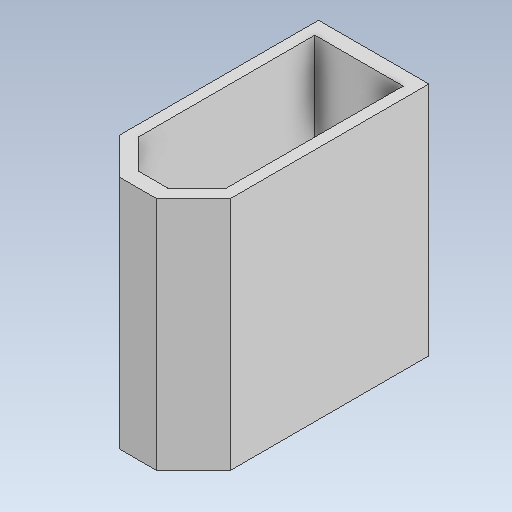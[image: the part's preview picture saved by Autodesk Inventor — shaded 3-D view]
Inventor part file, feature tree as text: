
AUTODESK INVENTOR PART (.ipt)
format: ipt  version: 2020 (Build 240168000, 168)  size: 100,352 bytes
history: native  units: in
note: dims shown in document units (in); Inventor stores cm internally (conversion verified against a paired STEP export)
features: other x3, sketch x2
ambient origin geometry x8: Origin, YZ Plane, XZ Plane, XY Plane, X Axis, Y Axis, Z Axis, Center Point
bodies: Solid1 (feature_tree)
feature tree (5):
  other  "TX60.ipt"
  other  "Solid1::TX60.ipt"
  other  "TaggingFeature1"
  sketch  "Sketch1"  dims[d0=0.3937in]
  sketch  "Sketch2"
